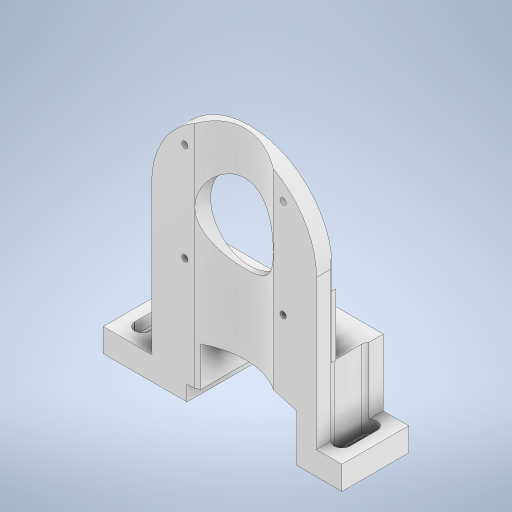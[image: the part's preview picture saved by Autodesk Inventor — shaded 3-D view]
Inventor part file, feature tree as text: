
AUTODESK INVENTOR PART (.ipt)
format: ipt  version: 2024 (Build 280153000, 153)  size: 504,832 bytes
history: native  units: mm
features: projected_geometry x11, extrude x10, sketch x10
ambient origin geometry x8: Origin, YZ Plane, XZ Plane, XY Plane, X Axis, Y Axis, Z Axis, Center Point
bodies: Solid1 (feature_tree)
feature tree (31):
  extrude  "Extrusion1"  Depth=5.4mm
  extrude  "Extrusion2"  Depth=60.0mm
  extrude  "Extrusion3"  Depth=50.8mm
  extrude  "Extrusion4"  Depth=12.5mm
  extrude  "Extrusion5"  Depth=7.5mm
  extrude  "Extrusion6"  TaperAngle=0.0deg  [1 undecoded]
  extrude  "Extrusion7"  Depth=10.0mm
  extrude  "Extrusion8"  Depth=45.0mm
  extrude  "Extrusion9"  Depth=105.0mm
  extrude  "Extrusion10"  TaperAngle=0.0deg  [1 undecoded]
  sketch  "Sketch1"  dims[d0=100.0mm d1=5.4mm]
  sketch  "Sketch2"  dims[d2=20.0mm d3=60.0mm]
  projected_geometry  "Projected Loop1"
  sketch  "Sketch3"  dims[d4=50.8mm d5=50.8mm]
  projected_geometry  "Projected Loop2"
  sketch  "Sketch4"  dims[d6=12.5mm d7=12.5mm]
  projected_geometry  "Projected Loop3"
  projected_geometry  "Projected Loop4"
  sketch  "Sketch5"  dims[d8=7.5mm d9=7.5mm]
  projected_geometry  "Projected Loop5"
  projected_geometry  "Projected Loop6"
  sketch  "Sketch6"  dims[d10=105.0mm d11=0.0mm]
  projected_geometry  "Projected Loop7"
  sketch  "Sketch7"  dims[d12=10.0mm d13=0.0mm d14=35.0mm]
  projected_geometry  "Projected Loop8"
  sketch  "Sketch8"  dims[d15=0.0mm d16=45.0mm]
  projected_geometry  "Projected Loop9"
  sketch  "Sketch9"  dims[d17=105.0mm d18=105.0mm]
  projected_geometry  "Projected Loop10"
  sketch  "Sketch10"  dims[d19=0.0mm d20=0.0mm d21=32.5mm d22=0.0mm d23=50.0mm d24=0.0mm d25=0.0mm d28=6.35mm d29=6.35mm d30=12.5mm d31=12.5mm d32=10.0mm d33=0.0mm d34=10.0mm d35=10.0mm d36=7.5mm d37=0.0mm d38=0.0mm d39=0.0mm d40=40.0mm d41=30.0mm d42=0.0mm d43=0.0mm d44=30.0mm d45=10.0mm d46=12.5mm d47=100.0mm d48=52.5mm d49=107.0mm d50=111.0mm d51=3.0mm d52=0.0mm d53=88.5mm d55=45.0deg d56=4.0mm d57=40.0mm d59=360.0deg d61=0.0mm d62=0.0mm d63=45.0mm d64=0.0mm d65=3.0mm d66=50.0mm d68=0.0mm d69=50.0mm d70=0.0mm d71=0.0mm d72=6.35mm d73=0.0mm d74=6.35mm d75=12.5mm d76=12.5mm d77=12.5mm d78=12.5mm]
  projected_geometry  "Projected Loop11"
note: 2 required parameter values undecoded (feature->parameter linkage not recoverable at this tier; creation-order binding heuristic only, values carry confidence <= 0.55)
